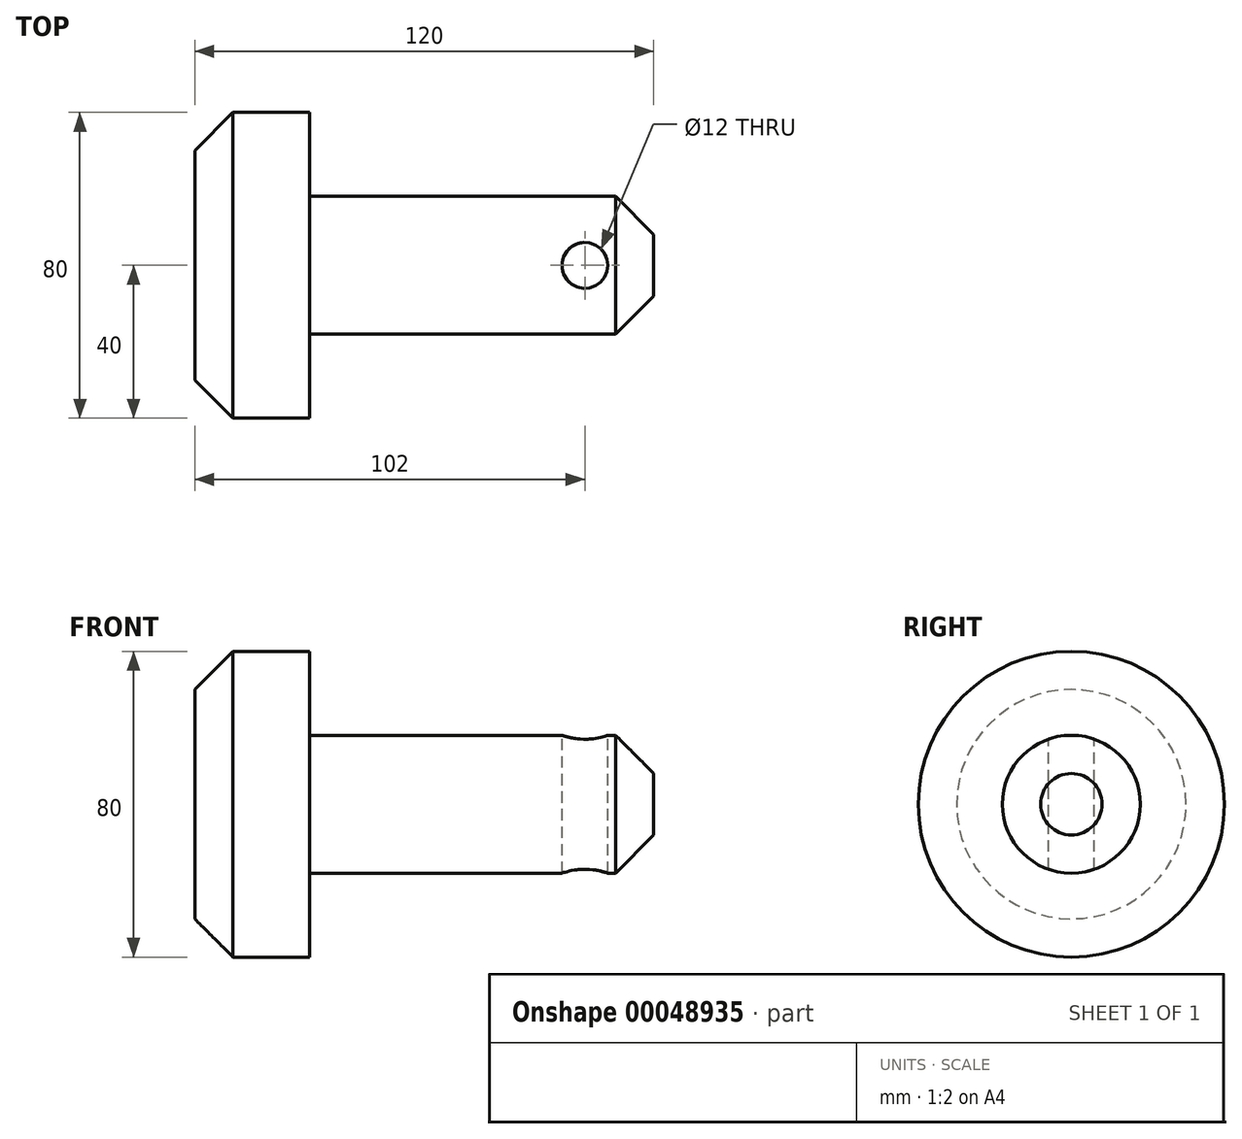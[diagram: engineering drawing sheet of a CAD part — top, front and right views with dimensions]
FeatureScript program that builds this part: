
annotation { "Feature Type Name" : "Feature", "Feature Type Description" : "" }
export const myFeature = defineFeature(function(context is Context, id is Id, definition is map)
    precondition{}
    {
        {
            var Q0;
            Q0=qCreatedBy(makeId("Top.planeOp"),FACE);
            var sketch = newSketch(context, id + "F0", { "sketchPlane" : qUnion([Q0])});
            skLineSegment(sketch, "E0", {"start": v(0, 0) * mm, "end": v(0, 40) * mm});
            skLineSegment(sketch, "E1", {"start": v(0, 40) * mm, "end": v(30, 40) * mm});
            skLineSegment(sketch, "E2", {"start": v(30, 40) * mm, "end": v(30, 18.04) * mm});
            skLineSegment(sketch, "E3", {"start": v(30, 18.04) * mm, "end": v(120, 18.04) * mm});
            skLineSegment(sketch, "E4", {"start": v(120, 18.04) * mm, "end": v(120, 0) * mm});
            skLineSegment(sketch, "E5", {"start": v(120, 0) * mm, "end": v(0, 0) * mm});
            skSolve(sketch);
        }
        {
            var Q0;
            Q0=makeQuery(id+"F0.imprint","IMPRINT",FACE,{"disambiguationData":[TD([[makeQuery(id+"F0.imprint","IMPRINT",EDGE,{"derivedFrom":sQuery(id+"F0.wireOp",EDGE,"E0")}),-1.0]])]});
            var Q1;
            Q1=sQuery(id+"F0.wireOp",EDGE,"E5");
            revolve(context, id + "F1", {"entities" : qUnion([Q0]), "axis" : qUnion([Q1]), "revolveType" : RevolveType.FULL});
        }
        {
            var Q0;
            Q0=makeQuery(id+"F1.opRevolve","SWEPT_EDGE",EDGE,{"disambiguationData":[OSD([sQuery(id+"F0.wireOp",EDGE,"E0"),sQuery(id+"F0.wireOp",EDGE,"E1")])]});
            var Q1;
            Q1=makeQuery(id+"F1.opRevolve","SWEPT_EDGE",EDGE,{"disambiguationData":[OSD([sQuery(id+"F0.wireOp",EDGE,"E3"),sQuery(id+"F0.wireOp",EDGE,"E4")])]});
            chamfer(context, id + "F2", {"entities" : qUnion([Q0, Q1]), "chamferType" : ChamferType.OFFSET_ANGLE, "width" : 10 * mm, "oppositeDirection" : false, "angle" : 45 * degree, "tangentPropagation" : true});
        }
        {
            var Q0;
            Q0=qCreatedBy(makeId("Top.planeOp"),FACE);
            var sketch = newSketch(context, id + "F3", { "sketchPlane" : qUnion([Q0])});
            skCircle(sketch, "E6", {"center": v(102, 0) * mm, "radius": 6 * mm});
            skSolve(sketch);
        }
        {
            var Q0;
            Q0 = qSketchRegion(id + "F3", true);
            extrude(context, id + "F4", {"entities" : qUnion([Q0]), "operationType" : NewBodyOperationType.REMOVE, "endBound" : BoundingType.THROUGH_ALL, "oppositeDirection" : true, "depth" : 25 * mm, "hasSecondDirection" : true, "secondDirectionBound" : SecondDirectionBoundingType.THROUGH_ALL, "secondDirectionOppositeDirection" : false, "secondDirectionDepth" : 25 * mm});
        }
    });
